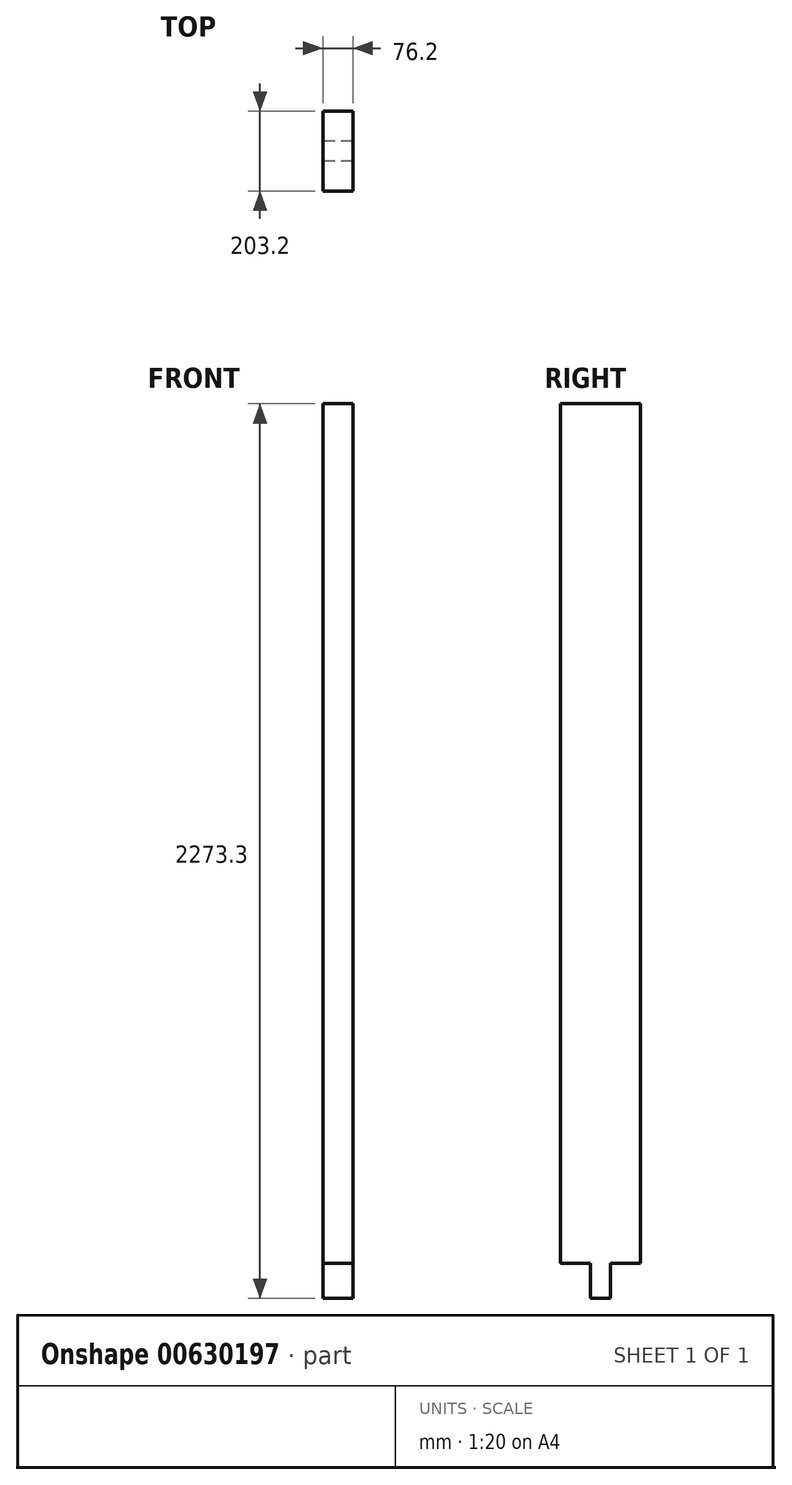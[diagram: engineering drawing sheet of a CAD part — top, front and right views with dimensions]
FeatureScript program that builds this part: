
annotation { "Feature Type Name" : "Feature", "Feature Type Description" : "" }
export const myFeature = defineFeature(function(context is Context, id is Id, definition is map)
    precondition{}
    {
        {
            var Q0;
            Q0=qCreatedBy(makeId("Right.planeOp"),FACE);
            var sketch = newSketch(context, id + "F0", { "sketchPlane" : qUnion([Q0])});
            skLineSegment(sketch, "E0.bottom", {"start": v(101.6, 1092.2) * mm, "end": v(-101.6, 1092.2) * mm});
            skLineSegment(sketch, "E0.top", {"start": v(101.6, -1092.2) * mm, "end": v(-101.6, -1092.2) * mm});
            skLineSegment(sketch, "E0.left", {"start": v(101.6, 1092.2) * mm, "end": v(101.6, -1092.2) * mm});
            skLineSegment(sketch, "E0.right", {"start": v(-101.6, 1092.2) * mm, "end": v(-101.6, -1092.2) * mm});
            skPoint(sketch, "E0.middle", {"position": v(0, 0) * mm});
            skLineSegment(sketch, "E1.bottom", {"start": v(25.4, -1181.1) * mm, "end": v(-25.4, -1181.1) * mm});
            skLineSegment(sketch, "E1.top", {"start": v(25.4, -1003.3) * mm, "end": v(-25.4, -1003.3) * mm});
            skLineSegment(sketch, "E1.left", {"start": v(25.4, -1181.1) * mm, "end": v(25.4, -1003.3) * mm});
            skLineSegment(sketch, "E1.right", {"start": v(-25.4, -1181.1) * mm, "end": v(-25.4, -1003.3) * mm});
            skPoint(sketch, "E1.middle", {"position": v(0, -1092.2) * mm});
            skSolve(sketch);
        }
        {
            var Q0;
            Q0 = qSketchRegion(id + "F0", true);
            extrude(context, id + "F1", {"entities" : qUnion([Q0]), "depth" : 76.2 * mm, "offsetDistance" : 25.4 * mm});
        }
    });
